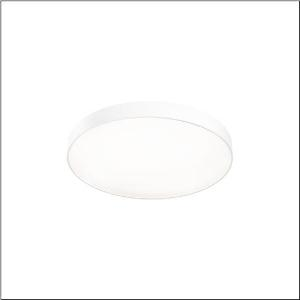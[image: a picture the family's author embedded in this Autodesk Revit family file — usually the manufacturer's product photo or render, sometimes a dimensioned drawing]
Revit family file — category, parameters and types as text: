
# Revit family: round_21_m_51mr36gm8421w
name_source: partatom
category: Lighting Fixtures
units: mm (PartAtom-declared; Revit-internal decimal feet)

## family parameters
Cut with Voids When Loaded = No
Host = Face
Light Source = No
Part Type = Normal
Room Calculation Point = No
Round Connector Dimension = Use Diameter
Shared = No

## types (1)
- --- (1 x LED, 8960 lm, 62.3 W, 4000K)
    Apparent Load = 62 VA
    CIE Flux Codes = 49 80 96 85 100
    Color Rendering = 80
    Color Temperature = 4000K
    Default Elevation = 1800 mm
    Description = Round 21 M, wall and ceiling luminaire, primary optical cover: cover, of PMMA, opal, light emission: direct/indirect distribution, primary light characteristic: symmetric, installation type: suspended mounting, surface-mounted, LED, rated luminous flux: 8.190lm, luminous efficacy: 135lm/W, light colour: 840, colour temperature: 4000K, control gear: ON/OFF Multilumen, with terminal, 3-pole, mains connection: 230V, AC, 50/60Hz, rated input power: 61W, housing, of aluminium, coated, white, diameter: 600mm, height: 62mm, protection rating (complete): IP40, insulation class (complete): insulation class I (protective earthing), certification: CE, impact resistance: IK04, permissible operating ambient temperature: -10..+35°C, packaging unit: 1 piece
    Height = 87 mm
    Lamp = 1 x LED
    Lamp Light Flux = 8960 lm
    Lamp Power = 62.3 W
    Lamp count = 1
    Length = 600 mm
    Luminous efficacy = 144 lm/W
    Manufacturer = Siteco
    ModVariant = No
    Model = 51MR36GM8421W
    Mounting Place = Ceiling
    Mounting Type = Surface mounted
    Number of Poles = 1
    OnlyDefault = Yes
    Power Factor = 1
    Product Name = Round 21 M
    Product group = wall and ceiling luminaire | ceiling mounted
    ProductGroupID = 304
    Protection Class = Protection class I
    Protection Degree = IP 40
    RLX_Detail_Level = 1
    RLX_Emergency_Light_Flux = 0 lm
    RLX_Emergency_Type = 0
    RLX_Emergency_Type_DB = No
    RlxData = <blob elided: 14833 chars, md5=0b5f347a>
    Socket = socket
    Standby Power = 0 W
    System Light Flux = 8960 lm
    System Power = 62 W
    Type Comments = factory setting: luminous flux: 100 % | (ON | ON | ON | ON) | 700 mA
    Type Image = l_1258330.jpg
    URL = http://relux.com
    VarID = @adj_040915
    Voltage = 0 V
    Weight = 0.00 kg
    Width = 0 mm  [stored 0 ft]

note: [stored X ft] marks values corroborated as IEEE doubles in the binary element streams (Revit-internal decimal feet)

## geometry (parser evidence)
native form markers: Sweep x13
no freeform markers — native parametric forms only
